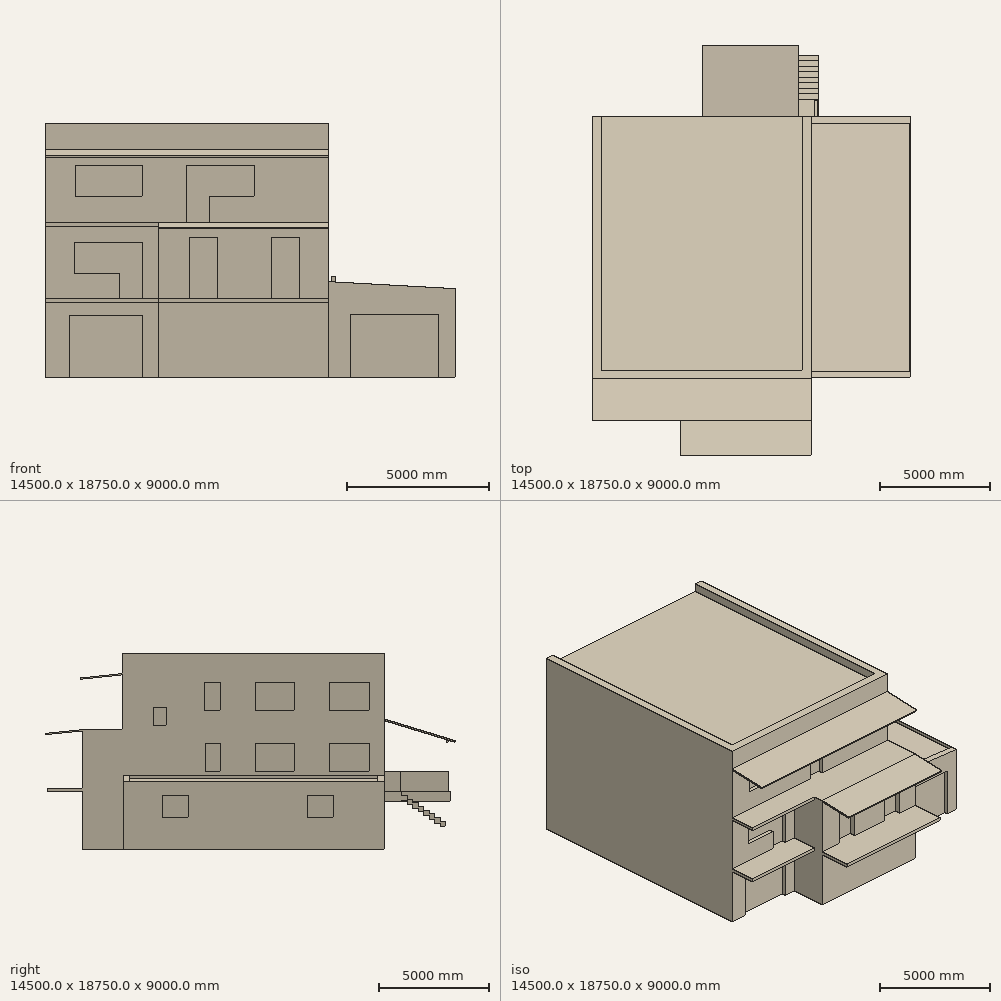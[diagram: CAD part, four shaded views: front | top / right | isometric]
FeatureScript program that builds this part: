
annotation { "Feature Type Name" : "Feature", "Feature Type Description" : "" }
export const myFeature = defineFeature(function(context is Context, id is Id, definition is map)
    precondition{}
    {
        {
            var Q0;
            Q0=qCreatedBy(makeId("Top.planeOp"),FACE);
            var sketch = newSketch(context, id + "F0", { "sketchPlane" : qUnion([Q0])});
            skLineSegment(sketch, "E0.bottom", {"start": v(-4506.26, 6009.06) * mm, "end": v(5493.74, 6009.06) * mm});
            skLineSegment(sketch, "E0.top", {"start": v(-4506.26, -5990.94) * mm, "end": v(5493.74, -5990.94) * mm});
            skLineSegment(sketch, "E0.left", {"start": v(-4506.26, 6009.06) * mm, "end": v(-4506.26, -5990.94) * mm});
            skLineSegment(sketch, "E0.right", {"start": v(5493.74, 6009.06) * mm, "end": v(5493.74, -5990.94) * mm});
            skLineSegment(sketch, "E1.bottom", {"start": v(5493.74, 6009.06) * mm, "end": v(9993.74, 6009.06) * mm});
            skLineSegment(sketch, "E1.top", {"start": v(5493.74, -5940.94) * mm, "end": v(9993.74, -5940.94) * mm});
            skLineSegment(sketch, "E1.left", {"start": v(5493.74, 6009.06) * mm, "end": v(5493.74, -5940.94) * mm});
            skLineSegment(sketch, "E1.right", {"start": v(9993.74, 6009.06) * mm, "end": v(9993.74, -5940.94) * mm});
            skSolve(sketch);
        }
        {
            var Q0;
            Q0=makeQuery(id+"F0.imprint","IMPRINT",FACE,{"disambiguationData":[TD([[makeQuery(id+"F0.imprint","IMPRINT",EDGE,{"derivedFrom":sQuery(id+"F0.wireOp",EDGE,"E0.bottom")}),-1.0]])]});
            extrude(context, id + "F1", {"entities" : qUnion([Q0]), "depth" : 9000 * mm});
        }
        {
            var Q0;
            Q0=makeQuery(id+"F0.imprint","IMPRINT",FACE,{"disambiguationData":[TD([[makeQuery(id+"F0.imprint","IMPRINT",EDGE,{"derivedFrom":sQuery(id+"F0.wireOp",EDGE,"E1.bottom")}),-1.0]])]});
            extrude(context, id + "F2", {"entities" : qUnion([Q0]), "operationType" : NewBodyOperationType.ADD, "depth" : 3400 * mm});
        }
        {
            var Q0;
            Q0=makeQuery(id+"F2.opExtrude","SWEPT_FACE",FACE,{"disambiguationData":[OSD([sQuery(id+"F0.wireOp",EDGE,"E1.top")])]});
            var sketch = newSketch(context, id + "F3", { "sketchPlane" : qUnion([Q0])});
            skLineSegment(sketch, "E2", {"start": v(5493.74, 3400) * mm, "end": v(9993.74, 3400) * mm});
            skLineSegment(sketch, "E3", {"start": v(9993.74, 3400) * mm, "end": v(9993.74, 3150) * mm});
            skLineSegment(sketch, "E4", {"start": v(9993.74, 3150) * mm, "end": v(5493.74, 3400) * mm});
            skSolve(sketch);
        }
        {
            var Q0;
            Q0=makeQuery(id+"F3.imprint","IMPRINT",FACE,{"disambiguationData":[TD([[makeQuery(id+"F3.imprint","IMPRINT",EDGE,{"derivedFrom":sQuery(id+"F3.wireOp",EDGE,"E2")}),-1.0]])]});
            extrude(context, id + "F4", {"entities" : qUnion([Q0]), "operationType" : NewBodyOperationType.REMOVE, "endBound" : BoundingType.THROUGH_ALL, "oppositeDirection" : true, "depth" : 25 * mm});
        }
        {
            var Q0;
            Q0=makeQuery(id+"F4.boolean.opBoolean","COPY",FACE,{"derivedFrom":makeQuery(id+"F4.opExtrude","SWEPT_FACE",FACE,{"disambiguationData":[OSD([sQuery(id+"F3.wireOp",EDGE,"E4")])]})});
            var sketch = newSketch(context, id + "F5", { "sketchPlane" : qUnion([Q0])});
            skLineSegment(sketch, "E5.bottom", {"start": v(9803.62, 5709.06) * mm, "end": v(5296.68, 5709.06) * mm});
            skLineSegment(sketch, "E5.top", {"start": v(9803.62, -5640.94) * mm, "end": v(5296.68, -5640.94) * mm});
            skLineSegment(sketch, "E5.left", {"start": v(9803.62, 5709.06) * mm, "end": v(9803.62, -5640.94) * mm});
            skLineSegment(sketch, "E5.right", {"start": v(5296.68, 5709.06) * mm, "end": v(5296.68, -5640.94) * mm});
            skSolve(sketch);
        }
        {
            var Q0;
            Q0=makeQuery(id+"F5.imprint","IMPRINT",FACE,{"disambiguationData":[TD([[makeQuery(id+"F5.imprint","IMPRINT",EDGE,{"derivedFrom":sQuery(id+"F5.wireOp",EDGE,"E5.bottom")}),1.0]])]});
            extrude(context, id + "F6", {"entities" : qUnion([Q0]), "operationType" : NewBodyOperationType.REMOVE, "oppositeDirection" : true, "depth" : 150 * mm});
        }
        {
            var Q0;
            Q0=makeQuery(id+"F2.opExtrude","SWEPT_FACE",FACE,{"disambiguationData":[OSD([sQuery(id+"F0.wireOp",EDGE,"E1.top")])]});
            var sketch = newSketch(context, id + "F7", { "sketchPlane" : qUnion([Q0])});
            skLineSegment(sketch, "E6.bottom", {"start": v(6293.74, 0) * mm, "end": v(9393.74, 0) * mm});
            skLineSegment(sketch, "E6.top", {"start": v(6293.74, 2250) * mm, "end": v(9393.74, 2250) * mm});
            skLineSegment(sketch, "E6.left", {"start": v(6293.74, 0) * mm, "end": v(6293.74, 2250) * mm});
            skLineSegment(sketch, "E6.right", {"start": v(9393.74, 0) * mm, "end": v(9393.74, 2250) * mm});
            skSolve(sketch);
        }
        {
            var Q0;
            Q0=makeQuery(id+"F7.imprint","IMPRINT",FACE,{"disambiguationData":[TD([[makeQuery(id+"F7.imprint","IMPRINT",EDGE,{"derivedFrom":sQuery(id+"F7.wireOp",EDGE,"E6.bottom")}),1.0]])]});
            extrude(context, id + "F8", {"entities" : qUnion([Q0]), "operationType" : NewBodyOperationType.REMOVE, "oppositeDirection" : true, "depth" : 150 * mm});
        }
        {
            var Q0;
            Q0=makeQuery(id+"F1.opExtrude","SWEPT_FACE",FACE,{"disambiguationData":[OSD([sQuery(id+"F0.wireOp",EDGE,"E0.top")])]});
            var sketch = newSketch(context, id + "F9", { "sketchPlane" : qUnion([Q0])});
            skLineSegment(sketch, "E7.bottom", {"start": v(5493.74, 0) * mm, "end": v(-506.26, 0) * mm});
            skLineSegment(sketch, "E7.top", {"start": v(5493.74, 5500) * mm, "end": v(-506.26, 5500) * mm});
            skLineSegment(sketch, "E7.left", {"start": v(5493.74, 0) * mm, "end": v(5493.74, 5500) * mm});
            skLineSegment(sketch, "E7.right", {"start": v(-506.26, 0) * mm, "end": v(-506.26, 5500) * mm});
            skSolve(sketch);
        }
        {
            var Q0;
            Q0 = qSketchRegion(id + "F9", true);
            extrude(context, id + "F10", {"entities" : qUnion([Q0]), "operationType" : NewBodyOperationType.ADD, "depth" : 1800 * mm});
        }
        {
            var Q0;
            Q0=makeQuery(id+"F10.opExtrude","CAP_FACE",FACE,{"disambiguationData":[OSD([sQuery(id+"F9.wireOp",EDGE,"E7.bottom"),sQuery(id+"F9.wireOp",EDGE,"E7.top"),sQuery(id+"F9.wireOp",EDGE,"E7.left"),sQuery(id+"F9.wireOp",EDGE,"E7.right")])],"isStart":false});
            var sketch = newSketch(context, id + "F11", { "sketchPlane" : qUnion([Q0])});
            skLineSegment(sketch, "E8.bottom", {"start": v(5493.74, 2800) * mm, "end": v(-506.26, 2800) * mm});
            skLineSegment(sketch, "E8.top", {"start": v(5493.74, 2650) * mm, "end": v(-506.26, 2650) * mm});
            skLineSegment(sketch, "E8.left", {"start": v(5493.74, 2800) * mm, "end": v(5493.74, 2650) * mm});
            skLineSegment(sketch, "E8.right", {"start": v(-506.26, 2800) * mm, "end": v(-506.26, 2650) * mm});
            skLineSegment(sketch, "E9.bottom", {"start": v(-506.26, 5500) * mm, "end": v(5493.74, 5500) * mm});
            skLineSegment(sketch, "E9.top", {"start": v(-506.26, 5350) * mm, "end": v(5493.74, 5350) * mm});
            skLineSegment(sketch, "E9.left", {"start": v(-506.26, 5500) * mm, "end": v(-506.26, 5350) * mm});
            skLineSegment(sketch, "E9.right", {"start": v(5493.74, 5500) * mm, "end": v(5493.74, 5350) * mm});
            skSolve(sketch);
        }
        {
            var Q0;
            Q0=makeQuery(id+"F11.imprint","IMPRINT",FACE,{"disambiguationData":[TD([[makeQuery(id+"F11.imprint","IMPRINT",EDGE,{"derivedFrom":sQuery(id+"F11.wireOp",EDGE,"E8.bottom")}),1.0]])]});
            extrude(context, id + "F12", {"entities" : qUnion([Q0]), "operationType" : NewBodyOperationType.ADD, "depth" : 1600 * mm});
        }
        {
            var Q0;
            Q0=makeQuery(id+"F1.opExtrude","SWEPT_FACE",FACE,{"disambiguationData":[OSD([sQuery(id+"F0.wireOp",EDGE,"E0.top")])]});
            var sketch = newSketch(context, id + "F13", { "sketchPlane" : qUnion([Q0])});
            skLineSegment(sketch, "E10.bottom", {"start": v(-506.26, 5500) * mm, "end": v(-4506.26, 5500) * mm});
            skLineSegment(sketch, "E10.top", {"start": v(-506.26, 5350) * mm, "end": v(-4506.26, 5350) * mm});
            skLineSegment(sketch, "E10.left", {"start": v(-506.26, 5500) * mm, "end": v(-506.26, 5350) * mm});
            skLineSegment(sketch, "E10.right", {"start": v(-4506.26, 5500) * mm, "end": v(-4506.26, 5350) * mm});
            skLineSegment(sketch, "E11.bottom", {"start": v(-4506.26, 2800) * mm, "end": v(-506.26, 2800) * mm});
            skLineSegment(sketch, "E11.top", {"start": v(-4506.26, 2650) * mm, "end": v(-506.26, 2650) * mm});
            skLineSegment(sketch, "E11.left", {"start": v(-4506.26, 2800) * mm, "end": v(-4506.26, 2650) * mm});
            skLineSegment(sketch, "E11.right", {"start": v(-506.26, 2800) * mm, "end": v(-506.26, 2650) * mm});
            skSolve(sketch);
        }
        {
            var Q0;
            Q0=makeQuery(id+"F13.imprint","IMPRINT",FACE,{"disambiguationData":[TD([[makeQuery(id+"F13.imprint","IMPRINT",EDGE,{"derivedFrom":sQuery(id+"F13.wireOp",EDGE,"E10.bottom")}),1.0]])]});
            var Q1;
            Q1=makeQuery(id+"F13.imprint","IMPRINT",FACE,{"disambiguationData":[TD([[makeQuery(id+"F13.imprint","IMPRINT",EDGE,{"derivedFrom":sQuery(id+"F13.wireOp",EDGE,"E11.bottom")}),-1.0]])]});
            extrude(context, id + "F14", {"entities" : qUnion([Q0, Q1]), "operationType" : NewBodyOperationType.ADD, "depth" : 1300 * mm});
        }
        {
            var Q0;
            Q0=makeQuery(id+"F12.boolean.opBoolean","MERGE",FACE,{"derivedFrom":[makeQuery(id+"F10.boolean.opBoolean","MERGE",FACE,{"derivedFrom":[makeQuery(id+"F1.opExtrude","SWEPT_FACE",FACE,{"disambiguationData":[OSD([sQuery(id+"F0.wireOp",EDGE,"E0.right"),sQuery(id+"F0.wireOp",EDGE,"E1.left")])]}),makeQuery(id+"F10.opExtrude","SWEPT_FACE",FACE,{"disambiguationData":[OSD([sQuery(id+"F9.wireOp",EDGE,"E7.left")])]})]}),makeQuery(id+"F12.opExtrude","SWEPT_FACE",FACE,{"disambiguationData":[OSD([sQuery(id+"F11.wireOp",EDGE,"E8.left")])]}),makeQuery(id+"F12.opExtrude","SWEPT_FACE",FACE,{"disambiguationData":[OSD([sQuery(id+"F11.wireOp",EDGE,"E9.right")])]})]});
            var sketch = newSketch(context, id + "F15", { "sketchPlane" : qUnion([Q0])});
            skLineSegment(sketch, "E12.bottom", {"start": v(-2190.94, 4867.43) * mm, "end": v(-1490.94, 4867.43) * mm});
            skLineSegment(sketch, "E12.top", {"start": v(-2190.94, 3567.43) * mm, "end": v(-1490.94, 3567.43) * mm});
            skLineSegment(sketch, "E12.left", {"start": v(-2190.94, 4867.43) * mm, "end": v(-2190.94, 3567.43) * mm});
            skLineSegment(sketch, "E12.right", {"start": v(-1490.94, 4867.43) * mm, "end": v(-1490.94, 3567.43) * mm});
            skLineSegment(sketch, "E13.bottom", {"start": v(109.06, 4867.43) * mm, "end": v(1909.06, 4867.43) * mm});
            skLineSegment(sketch, "E13.top", {"start": v(109.06, 3567.43) * mm, "end": v(1909.06, 3567.43) * mm});
            skLineSegment(sketch, "E13.left", {"start": v(109.06, 4867.43) * mm, "end": v(109.06, 3567.43) * mm});
            skLineSegment(sketch, "E13.right", {"start": v(1909.06, 4867.43) * mm, "end": v(1909.06, 3567.43) * mm});
            skLineSegment(sketch, "E14.bottom", {"start": v(3509.06, 4867.43) * mm, "end": v(5309.06, 4867.43) * mm});
            skLineSegment(sketch, "E14.top", {"start": v(3509.06, 3567.43) * mm, "end": v(5309.06, 3567.43) * mm});
            skLineSegment(sketch, "E14.left", {"start": v(3509.06, 4867.43) * mm, "end": v(3509.06, 3567.43) * mm});
            skLineSegment(sketch, "E14.right", {"start": v(5309.06, 4867.43) * mm, "end": v(5309.06, 3567.43) * mm});
            skLineSegment(sketch, "E15.bottom", {"start": v(109.06, 6367.43) * mm, "end": v(1909.06, 6367.43) * mm});
            skLineSegment(sketch, "E15.top", {"start": v(109.06, 7667.43) * mm, "end": v(1909.06, 7667.43) * mm});
            skLineSegment(sketch, "E15.left", {"start": v(109.06, 6367.43) * mm, "end": v(109.06, 7667.43) * mm});
            skLineSegment(sketch, "E15.right", {"start": v(1909.06, 6367.43) * mm, "end": v(1909.06, 7667.43) * mm});
            skLineSegment(sketch, "E16.bottom", {"start": v(3509.06, 6367.43) * mm, "end": v(5309.06, 6367.43) * mm});
            skLineSegment(sketch, "E16.top", {"start": v(3509.06, 7667.43) * mm, "end": v(5309.06, 7667.43) * mm});
            skLineSegment(sketch, "E16.left", {"start": v(3509.06, 6367.43) * mm, "end": v(3509.06, 7667.43) * mm});
            skLineSegment(sketch, "E16.right", {"start": v(5309.06, 6367.43) * mm, "end": v(5309.06, 7667.43) * mm});
            skLineSegment(sketch, "E17.bottom", {"start": v(-1490.94, 6367.43) * mm, "end": v(-2240.55, 6367.43) * mm});
            skLineSegment(sketch, "E17.top", {"start": v(-1490.94, 7667.43) * mm, "end": v(-2240.55, 7667.43) * mm});
            skLineSegment(sketch, "E17.left", {"start": v(-1490.94, 6367.43) * mm, "end": v(-1490.94, 7667.43) * mm});
            skLineSegment(sketch, "E17.right", {"start": v(-2240.55, 6367.43) * mm, "end": v(-2240.55, 7667.43) * mm});
            skLineSegment(sketch, "E18.bottom", {"start": v(-4545.24, 6502.32) * mm, "end": v(-3968.61, 6502.32) * mm});
            skLineSegment(sketch, "E18.top", {"start": v(-4545.24, 5695.04) * mm, "end": v(-3968.61, 5695.04) * mm});
            skLineSegment(sketch, "E18.left", {"start": v(-4545.24, 6502.32) * mm, "end": v(-4545.24, 5695.04) * mm});
            skLineSegment(sketch, "E18.right", {"start": v(-3968.61, 6502.32) * mm, "end": v(-3968.61, 5695.04) * mm});
            skSolve(sketch);
        }
        {
            var Q0;
            Q0=makeQuery(id+"F15.imprint","IMPRINT",FACE,{"disambiguationData":[TD([[makeQuery(id+"F15.imprint","IMPRINT",EDGE,{"derivedFrom":sQuery(id+"F15.wireOp",EDGE,"E18.bottom")}),-1.0]])]});
            var Q1;
            Q1=makeQuery(id+"F15.imprint","IMPRINT",FACE,{"disambiguationData":[TD([[makeQuery(id+"F15.imprint","IMPRINT",EDGE,{"derivedFrom":sQuery(id+"F15.wireOp",EDGE,"E17.bottom")}),-1.0]])]});
            var Q2;
            Q2=makeQuery(id+"F15.imprint","IMPRINT",FACE,{"disambiguationData":[TD([[makeQuery(id+"F15.imprint","IMPRINT",EDGE,{"derivedFrom":sQuery(id+"F15.wireOp",EDGE,"E15.bottom")}),1.0]])]});
            var Q3;
            Q3=makeQuery(id+"F15.imprint","IMPRINT",FACE,{"disambiguationData":[TD([[makeQuery(id+"F15.imprint","IMPRINT",EDGE,{"derivedFrom":sQuery(id+"F15.wireOp",EDGE,"E16.bottom")}),1.0]])]});
            var Q4;
            Q4=makeQuery(id+"F15.imprint","IMPRINT",FACE,{"disambiguationData":[TD([[makeQuery(id+"F15.imprint","IMPRINT",EDGE,{"derivedFrom":sQuery(id+"F15.wireOp",EDGE,"E14.bottom")}),-1.0]])]});
            var Q5;
            Q5=makeQuery(id+"F15.imprint","IMPRINT",FACE,{"disambiguationData":[TD([[makeQuery(id+"F15.imprint","IMPRINT",EDGE,{"derivedFrom":sQuery(id+"F15.wireOp",EDGE,"E13.bottom")}),-1.0]])]});
            var Q6;
            Q6=makeQuery(id+"F15.imprint","IMPRINT",FACE,{"disambiguationData":[TD([[makeQuery(id+"F15.imprint","IMPRINT",EDGE,{"derivedFrom":sQuery(id+"F15.wireOp",EDGE,"E12.bottom")}),-1.0]])]});
            extrude(context, id + "F16", {"entities" : qUnion([Q0, Q1, Q2, Q3, Q4, Q5, Q6]), "operationType" : NewBodyOperationType.REMOVE, "oppositeDirection" : true, "depth" : 200 * mm});
        }
        {
            var Q0;
            Q0=makeQuery(id+"F2.opExtrude","SWEPT_FACE",FACE,{"disambiguationData":[OSD([sQuery(id+"F0.wireOp",EDGE,"E1.right")])]});
            var sketch = newSketch(context, id + "F17", { "sketchPlane" : qUnion([Q0])});
            skLineSegment(sketch, "E19.bottom", {"start": v(-4154.46, 2500) * mm, "end": v(-2954.46, 2500) * mm});
            skLineSegment(sketch, "E19.top", {"start": v(-4154.46, 1500) * mm, "end": v(-2954.46, 1500) * mm});
            skLineSegment(sketch, "E19.left", {"start": v(-4154.46, 2500) * mm, "end": v(-4154.46, 1500) * mm});
            skLineSegment(sketch, "E19.right", {"start": v(-2954.46, 2500) * mm, "end": v(-2954.46, 1500) * mm});
            skLineSegment(sketch, "E20.bottom", {"start": v(2485.6, 2500) * mm, "end": v(3685.6, 2500) * mm});
            skLineSegment(sketch, "E20.top", {"start": v(2485.6, 1500) * mm, "end": v(3685.6, 1500) * mm});
            skLineSegment(sketch, "E20.left", {"start": v(2485.6, 2500) * mm, "end": v(2485.6, 1500) * mm});
            skLineSegment(sketch, "E20.right", {"start": v(3685.6, 2500) * mm, "end": v(3685.6, 1500) * mm});
            skSolve(sketch);
        }
        {
            var Q0;
            Q0=makeQuery(id+"F17.imprint","IMPRINT",FACE,{"disambiguationData":[TD([[makeQuery(id+"F17.imprint","IMPRINT",EDGE,{"derivedFrom":sQuery(id+"F17.wireOp",EDGE,"E19.bottom")}),-1.0]])]});
            var Q1;
            Q1=makeQuery(id+"F17.imprint","IMPRINT",FACE,{"disambiguationData":[TD([[makeQuery(id+"F17.imprint","IMPRINT",EDGE,{"derivedFrom":sQuery(id+"F17.wireOp",EDGE,"E20.bottom")}),-1.0]])]});
            extrude(context, id + "F18", {"entities" : qUnion([Q0, Q1]), "operationType" : NewBodyOperationType.REMOVE, "oppositeDirection" : true, "depth" : 200 * mm});
        }
        {
            var Q0;
            {var subQ2=sQuery(id+"F0.wireOp",EDGE,"E0.top");Q0=makeQuery(id+"F14.boolean.opBoolean","SPLIT",FACE,{"disambiguationData":[TD([makeQuery(id+"F10.opExtrude","SWEPT_FACE",FACE,{"disambiguationData":[OSD([sQuery(id+"F9.wireOp",EDGE,"E7.bottom")])]})])],"derivedFrom":makeQuery(id+"F1.opExtrude","SWEPT_FACE",FACE,{"disambiguationData":[OSD([subQ2])]})});}
            var sketch = newSketch(context, id + "F19", { "sketchPlane" : qUnion([Q0])});
            skLineSegment(sketch, "E21.bottom", {"start": v(-3641.41, 2200) * mm, "end": v(-1090.82, 2200) * mm});
            skLineSegment(sketch, "E21.top", {"start": v(-3641.41, 0) * mm, "end": v(-1090.82, 0) * mm});
            skLineSegment(sketch, "E21.left", {"start": v(-3641.41, 2200) * mm, "end": v(-3641.41, 0) * mm});
            skLineSegment(sketch, "E21.right", {"start": v(-1090.82, 2200) * mm, "end": v(-1090.82, 0) * mm});
            skSolve(sketch);
        }
        {
            var Q0;
            Q0=makeQuery(id+"F19.imprint","IMPRINT",FACE,{"disambiguationData":[TD([[makeQuery(id+"F19.imprint","IMPRINT",EDGE,{"derivedFrom":sQuery(id+"F19.wireOp",EDGE,"E21.bottom")}),-1.0]])]});
            extrude(context, id + "F20", {"entities" : qUnion([Q0]), "operationType" : NewBodyOperationType.REMOVE, "oppositeDirection" : true, "depth" : 200 * mm});
        }
        {
            var Q0;
            Q0=makeQuery(id+"F1.opExtrude","CAP_FACE",FACE,{"disambiguationData":[OSD([sQuery(id+"F0.wireOp",EDGE,"E0.bottom"),sQuery(id+"F0.wireOp",EDGE,"E0.top"),sQuery(id+"F0.wireOp",EDGE,"E0.left"),sQuery(id+"F0.wireOp",EDGE,"E0.right"),sQuery(id+"F0.wireOp",EDGE,"E1.left")])],"isStart":false});
            var sketch = newSketch(context, id + "F21", { "sketchPlane" : qUnion([Q0])});
            skLineSegment(sketch, "E22.bottom", {"start": v(-4106.26, 6009.06) * mm, "end": v(5093.74, 6009.06) * mm});
            skLineSegment(sketch, "E22.top", {"start": v(-4106.26, -5590.94) * mm, "end": v(5093.74, -5590.94) * mm});
            skLineSegment(sketch, "E22.left", {"start": v(-4106.26, 6009.06) * mm, "end": v(-4106.26, -5590.94) * mm});
            skLineSegment(sketch, "E22.right", {"start": v(5093.74, 6009.06) * mm, "end": v(5093.74, -5590.94) * mm});
            skSolve(sketch);
        }
        {
            var Q0;
            Q0 = qSketchRegion(id + "F21", true);
            extrude(context, id + "F22", {"entities" : qUnion([Q0]), "operationType" : NewBodyOperationType.REMOVE, "oppositeDirection" : true, "depth" : 400 * mm});
        }
        {
            var Q0;
            {var subQ0=sQuery(id+"F9.wireOp",EDGE,"E7.left");var subQ1=sQuery(id+"F9.wireOp",EDGE,"E7.right");Q0=makeQuery(id+"F12.boolean.opBoolean","SPLIT",FACE,{"disambiguationData":[TD([makeQuery(id+"F12.opExtrude","SWEPT_FACE",FACE,{"disambiguationData":[OSD([sQuery(id+"F11.wireOp",EDGE,"E8.bottom")])]})])],"derivedFrom":makeQuery(id+"F10.opExtrude","CAP_FACE",FACE,{"disambiguationData":[OSD([sQuery(id+"F9.wireOp",EDGE,"E7.bottom"),sQuery(id+"F9.wireOp",EDGE,"E7.top"),subQ0,subQ1])],"isStart":false})});}
            var sketch = newSketch(context, id + "F23", { "sketchPlane" : qUnion([Q0])});
            skLineSegment(sketch, "E23.bottom", {"start": v(581.4, 4950) * mm, "end": v(1581.4, 4950) * mm});
            skLineSegment(sketch, "E23.top", {"start": v(581.4, 2800) * mm, "end": v(1581.4, 2800) * mm});
            skLineSegment(sketch, "E23.left", {"start": v(581.4, 4950) * mm, "end": v(581.4, 2800) * mm});
            skLineSegment(sketch, "E23.right", {"start": v(1581.4, 4950) * mm, "end": v(1581.4, 2800) * mm});
            skLineSegment(sketch, "E24.bottom", {"start": v(3481.4, 2800) * mm, "end": v(4481.4, 2800) * mm});
            skLineSegment(sketch, "E24.top", {"start": v(3481.4, 4950) * mm, "end": v(4481.4, 4950) * mm});
            skLineSegment(sketch, "E24.left", {"start": v(3481.4, 2800) * mm, "end": v(3481.4, 4950) * mm});
            skLineSegment(sketch, "E24.right", {"start": v(4481.4, 2800) * mm, "end": v(4481.4, 4950) * mm});
            skSolve(sketch);
        }
        {
            var Q0;
            Q0=makeQuery(id+"F23.imprint","IMPRINT",FACE,{"disambiguationData":[TD([[makeQuery(id+"F23.imprint","IMPRINT",EDGE,{"derivedFrom":sQuery(id+"F23.wireOp",EDGE,"E24.bottom")}),-1.0]])]});
            var Q1;
            Q1=makeQuery(id+"F23.imprint","IMPRINT",FACE,{"disambiguationData":[TD([[makeQuery(id+"F23.imprint","IMPRINT",EDGE,{"derivedFrom":sQuery(id+"F23.wireOp",EDGE,"E23.bottom")}),-1.0]])]});
            extrude(context, id + "F24", {"entities" : qUnion([Q0, Q1]), "operationType" : NewBodyOperationType.REMOVE, "oppositeDirection" : true, "depth" : 300 * mm});
        }
        {
            var Q0;
            {var subQ3=sQuery(id+"F0.wireOp",EDGE,"E0.top");Q0=makeQuery(id+"F14.boolean.opBoolean","SPLIT",FACE,{"disambiguationData":[TD([makeQuery(id+"F10.opExtrude","SWEPT_FACE",FACE,{"disambiguationData":[OSD([sQuery(id+"F9.wireOp",EDGE,"E7.top")])]})])],"derivedFrom":makeQuery(id+"F1.opExtrude","SWEPT_FACE",FACE,{"disambiguationData":[OSD([subQ3])]})});}
            var sketch = newSketch(context, id + "F25", { "sketchPlane" : qUnion([Q0])});
            skLineSegment(sketch, "E25.bottom", {"start": v(2893.74, 7500) * mm, "end": v(1293.74, 7500) * mm});
            skLineSegment(sketch, "E25.top", {"start": v(2893.74, 6400) * mm, "end": v(1293.74, 6400) * mm});
            skLineSegment(sketch, "E25.left", {"start": v(2893.74, 7500) * mm, "end": v(2893.74, 6400) * mm});
            skLineSegment(sketch, "E25.right", {"start": v(1293.74, 7500) * mm, "end": v(1293.74, 6400) * mm});
            skLineSegment(sketch, "E26.bottom", {"start": v(1293.74, 7500) * mm, "end": v(493.74, 7500) * mm});
            skLineSegment(sketch, "E26.top", {"start": v(1293.74, 5500) * mm, "end": v(493.74, 5500) * mm});
            skLineSegment(sketch, "E26.left", {"start": v(1293.74, 7500) * mm, "end": v(1293.74, 5500) * mm});
            skLineSegment(sketch, "E26.right", {"start": v(493.74, 7500) * mm, "end": v(493.74, 5500) * mm});
            skLineSegment(sketch, "E27.bottom", {"start": v(-1088.33, 6400) * mm, "end": v(-3428.85, 6400) * mm});
            skLineSegment(sketch, "E27.top", {"start": v(-1088.33, 7500) * mm, "end": v(-3428.85, 7500) * mm});
            skLineSegment(sketch, "E27.left", {"start": v(-1088.33, 6400) * mm, "end": v(-1088.33, 7500) * mm});
            skLineSegment(sketch, "E27.right", {"start": v(-3428.85, 6400) * mm, "end": v(-3428.85, 7500) * mm});
            skLineSegment(sketch, "E28.bottom", {"start": v(-1088.33, 4800) * mm, "end": v(-1888.33, 4800) * mm});
            skLineSegment(sketch, "E28.top", {"start": v(-1088.33, 2800) * mm, "end": v(-1888.33, 2800) * mm});
            skLineSegment(sketch, "E28.left", {"start": v(-1088.33, 4800) * mm, "end": v(-1088.33, 2800) * mm});
            skLineSegment(sketch, "E28.right", {"start": v(-1888.33, 4800) * mm, "end": v(-1888.33, 2800) * mm});
            skLineSegment(sketch, "E29.bottom", {"start": v(-3488.33, 4800) * mm, "end": v(-1888.33, 4800) * mm});
            skLineSegment(sketch, "E29.top", {"start": v(-3488.33, 3700) * mm, "end": v(-1888.33, 3700) * mm});
            skLineSegment(sketch, "E29.left", {"start": v(-3488.33, 4800) * mm, "end": v(-3488.33, 3700) * mm});
            skLineSegment(sketch, "E29.right", {"start": v(-1888.33, 4800) * mm, "end": v(-1888.33, 3700) * mm});
            skSolve(sketch);
        }
        {
            var Q0;
            Q0=makeQuery(id+"F25.imprint","IMPRINT",FACE,{"disambiguationData":[TD([[makeQuery(id+"F25.imprint","IMPRINT",EDGE,{"derivedFrom":sQuery(id+"F25.wireOp",EDGE,"E27.bottom")}),-1.0]])]});
            var Q1;
            {var subQ1=sQuery(id+"F25.wireOp",EDGE,"E26.bottom");Q1=makeQuery(id+"F25.imprint","IMPRINT",FACE,{"disambiguationData":[TD([[makeQuery(id+"F25.imprint","IMPRINT",EDGE,{"derivedFrom":subQ1}),1.0]])]});}
            var Q2;
            {var subQ0=sQuery(id+"F25.wireOp",EDGE,"E25.bottom");Q2=makeQuery(id+"F25.imprint","IMPRINT",FACE,{"disambiguationData":[TD([[makeQuery(id+"F25.imprint","IMPRINT",EDGE,{"derivedFrom":subQ0}),1.0]])]});}
            var Q3;
            Q3=makeQuery(id+"F25.imprint","IMPRINT",FACE,{"disambiguationData":[TD([[makeQuery(id+"F25.imprint","IMPRINT",EDGE,{"derivedFrom":sQuery(id+"F25.wireOp",EDGE,"E28.bottom")}),1.0]])]});
            var Q4;
            Q4=makeQuery(id+"F25.imprint","IMPRINT",FACE,{"disambiguationData":[TD([[makeQuery(id+"F25.imprint","IMPRINT",EDGE,{"derivedFrom":sQuery(id+"F25.wireOp",EDGE,"E29.bottom")}),-1.0]])]});
            extrude(context, id + "F26", {"entities" : qUnion([Q0, Q1, Q2, Q3, Q4]), "operationType" : NewBodyOperationType.REMOVE, "oppositeDirection" : true, "depth" : 200 * mm});
        }
        {
            var Q0;
            Q0=makeQuery(id+"F12.boolean.opBoolean","MERGE",FACE,{"derivedFrom":[makeQuery(id+"F10.boolean.opBoolean","MERGE",FACE,{"derivedFrom":[makeQuery(id+"F1.opExtrude","SWEPT_FACE",FACE,{"disambiguationData":[OSD([sQuery(id+"F0.wireOp",EDGE,"E0.right"),sQuery(id+"F0.wireOp",EDGE,"E1.left")])]}),makeQuery(id+"F10.opExtrude","SWEPT_FACE",FACE,{"disambiguationData":[OSD([sQuery(id+"F9.wireOp",EDGE,"E7.left")])]})]}),makeQuery(id+"F12.opExtrude","SWEPT_FACE",FACE,{"disambiguationData":[OSD([sQuery(id+"F11.wireOp",EDGE,"E8.left")])]}),makeQuery(id+"F12.opExtrude","SWEPT_FACE",FACE,{"disambiguationData":[OSD([sQuery(id+"F11.wireOp",EDGE,"E9.right")])]})]});
            var sketch = newSketch(context, id + "F27", { "sketchPlane" : qUnion([Q0])});
            skLineSegment(sketch, "E30", {"start": v(-5990.94, 8059.67) * mm, "end": v(-7890.94, 7859.67) * mm});
            skLineSegment(sketch, "E31", {"start": v(-7890.94, 7859.67) * mm, "end": v(-7884.66, 7800) * mm});
            skLineSegment(sketch, "E32", {"start": v(-7884.66, 7800) * mm, "end": v(-5990.94, 7999.34) * mm});
            skSolve(sketch);
        }
        {
            var Q0;
            {var subQ0=sQuery(id+"F27.wireOp",EDGE,"E30");Q0=makeQuery(id+"F27.imprint","IMPRINT",FACE,{"disambiguationData":[TD([[makeQuery(id+"F27.imprint","IMPRINT",EDGE,{"derivedFrom":subQ0}),1.0]])]});}
            var Q1;
            Q1=makeQuery(id+"F14.boolean.opBoolean","MERGE",FACE,{"derivedFrom":[makeQuery(id+"F1.opExtrude","SWEPT_FACE",FACE,{"disambiguationData":[OSD([sQuery(id+"F0.wireOp",EDGE,"E0.left")])]}),makeQuery(id+"F14.opExtrude","SWEPT_FACE",FACE,{"disambiguationData":[OSD([sQuery(id+"F13.wireOp",EDGE,"E10.right")])]}),makeQuery(id+"F14.opExtrude","SWEPT_FACE",FACE,{"disambiguationData":[OSD([sQuery(id+"F13.wireOp",EDGE,"E11.left")])]})]});
            extrude(context, id + "F28", {"entities" : qUnion([Q0]), "operationType" : NewBodyOperationType.ADD, "endBound" : BoundingType.UP_TO_SURFACE, "oppositeDirection" : true, "endBoundEntityFace" : qUnion([Q1]), "depth" : 25 * mm});
        }
        {
            var Q0;
            {var subQ0=sQuery(id+"F0.wireOp",EDGE,"E0.right");Q0=makeQuery(id+"F28.boolean.opBoolean","MERGE",FACE,{"derivedFrom":[makeQuery(id+"F12.boolean.opBoolean","MERGE",FACE,{"derivedFrom":[makeQuery(id+"F10.boolean.opBoolean","MERGE",FACE,{"derivedFrom":[makeQuery(id+"F1.opExtrude","SWEPT_FACE",FACE,{"disambiguationData":[OSD([subQ0,sQuery(id+"F0.wireOp",EDGE,"E1.left")])]}),makeQuery(id+"F10.opExtrude","SWEPT_FACE",FACE,{"disambiguationData":[OSD([sQuery(id+"F9.wireOp",EDGE,"E7.left")])]})]}),makeQuery(id+"F12.opExtrude","SWEPT_FACE",FACE,{"disambiguationData":[OSD([sQuery(id+"F11.wireOp",EDGE,"E8.left")])]})]}),makeQuery(id+"F28.opExtrude","CAP_FACE",FACE,{"disambiguationData":[OSD([sQuery(id+"F0.wireOp",EDGE,"E0.top"),subQ0,sQuery(id+"F27.wireOp",EDGE,"E30"),sQuery(id+"F27.wireOp",EDGE,"E31"),sQuery(id+"F27.wireOp",EDGE,"E32")])],"isStart":true})]});}
            var sketch = newSketch(context, id + "F29", { "sketchPlane" : qUnion([Q0])});
            skLineSegment(sketch, "E33", {"start": v(-7790.94, 5500) * mm, "end": v(-9490.94, 5330) * mm});
            skLineSegment(sketch, "E34", {"start": v(-9490.94, 5330) * mm, "end": v(-9484.97, 5270.3) * mm});
            skLineSegment(sketch, "E35", {"start": v(-9484.97, 5270.3) * mm, "end": v(-7790.94, 5439.7) * mm});
            skSolve(sketch);
        }
        {
            var Q0;
            {var subQ0=sQuery(id+"F29.wireOp",EDGE,"E33");Q0=makeQuery(id+"F29.imprint","IMPRINT",FACE,{"disambiguationData":[TD([[makeQuery(id+"F29.imprint","IMPRINT",EDGE,{"derivedFrom":subQ0}),1.0]])]});}
            var Q1;
            Q1=makeQuery(id+"F12.boolean.opBoolean","MERGE",FACE,{"derivedFrom":[makeQuery(id+"F10.opExtrude","SWEPT_FACE",FACE,{"disambiguationData":[OSD([sQuery(id+"F9.wireOp",EDGE,"E7.right")])]}),makeQuery(id+"F12.opExtrude","SWEPT_FACE",FACE,{"disambiguationData":[OSD([sQuery(id+"F11.wireOp",EDGE,"E8.right")])]})]});
            extrude(context, id + "F30", {"entities" : qUnion([Q0]), "operationType" : NewBodyOperationType.ADD, "endBound" : BoundingType.UP_TO_SURFACE, "oppositeDirection" : true, "endBoundEntityFace" : qUnion([Q1]), "depth" : 25 * mm});
        }
        {
            var Q0;
            Q0=makeQuery(id+"F2.boolean.opBoolean","MERGE",FACE,{"derivedFrom":[makeQuery(id+"F1.opExtrude","SWEPT_FACE",FACE,{"disambiguationData":[OSD([sQuery(id+"F0.wireOp",EDGE,"E0.bottom")])]}),makeQuery(id+"F2.opExtrude","SWEPT_FACE",FACE,{"disambiguationData":[OSD([sQuery(id+"F0.wireOp",EDGE,"E1.bottom")])]})]});
            var sketch = newSketch(context, id + "F31", { "sketchPlane" : qUnion([Q0])});
            skLineSegment(sketch, "E36.bottom", {"start": v(-8108.12, 2400) * mm, "end": v(-6908.12, 2400) * mm});
            skLineSegment(sketch, "E36.top", {"start": v(-8108.12, 1400) * mm, "end": v(-6908.12, 1400) * mm});
            skLineSegment(sketch, "E36.left", {"start": v(-8108.12, 2400) * mm, "end": v(-8108.12, 1400) * mm});
            skLineSegment(sketch, "E36.right", {"start": v(-6908.12, 2400) * mm, "end": v(-6908.12, 1400) * mm});
            skSolve(sketch);
        }
        {
            var Q0;
            Q0=makeQuery(id+"F31.imprint","IMPRINT",FACE,{"disambiguationData":[TD([[makeQuery(id+"F31.imprint","IMPRINT",EDGE,{"derivedFrom":sQuery(id+"F31.wireOp",EDGE,"E36.bottom")}),-1.0]])]});
            extrude(context, id + "F32", {"entities" : qUnion([Q0]), "operationType" : NewBodyOperationType.REMOVE, "oppositeDirection" : true, "depth" : 200 * mm});
        }
        {
            var Q0;
            Q0=makeQuery(id+"F2.boolean.opBoolean","MERGE",FACE,{"derivedFrom":[makeQuery(id+"F1.opExtrude","SWEPT_FACE",FACE,{"disambiguationData":[OSD([sQuery(id+"F0.wireOp",EDGE,"E0.bottom")])]}),makeQuery(id+"F2.opExtrude","SWEPT_FACE",FACE,{"disambiguationData":[OSD([sQuery(id+"F0.wireOp",EDGE,"E1.bottom")])]})]});
            var sketch = newSketch(context, id + "F33", { "sketchPlane" : qUnion([Q0])});
            skPoint(sketch, "E37", {"position": v(-4893.74, 2667.43) * mm});
            skLineSegment(sketch, "E38.bottom", {"start": v(-4893.74, 2667.43) * mm, "end": v(-493.74, 2667.43) * mm});
            skLineSegment(sketch, "E38.top", {"start": v(-4893.74, 2217.43) * mm, "end": v(-493.74, 2217.43) * mm});
            skLineSegment(sketch, "E38.left", {"start": v(-4893.74, 2667.43) * mm, "end": v(-4893.74, 2217.43) * mm});
            skLineSegment(sketch, "E38.right", {"start": v(-493.74, 2667.43) * mm, "end": v(-493.74, 2217.43) * mm});
            skSolve(sketch);
        }
        {
            var Q0;
            Q0 = qSketchRegion(id + "F33", true);
            extrude(context, id + "F34", {"entities" : qUnion([Q0]), "operationType" : NewBodyOperationType.ADD, "depth" : 3000 * mm, "offsetDistance" : 25 * mm});
        }
        {
            var Q0;
            Q0=makeQuery(id+"F2.boolean.opBoolean","MERGE",FACE,{"derivedFrom":[makeQuery(id+"F1.opExtrude","SWEPT_FACE",FACE,{"disambiguationData":[OSD([sQuery(id+"F0.wireOp",EDGE,"E0.bottom")])]}),makeQuery(id+"F2.opExtrude","SWEPT_FACE",FACE,{"disambiguationData":[OSD([sQuery(id+"F0.wireOp",EDGE,"E1.bottom")])]})]});
            var sketch = newSketch(context, id + "F35", { "sketchPlane" : qUnion([Q0])});
            skLineSegment(sketch, "E39.bottom", {"start": v(-3993.74, 2717.43) * mm, "end": v(-2593.74, 2717.43) * mm});
            skLineSegment(sketch, "E39.top", {"start": v(-3993.74, 4817.43) * mm, "end": v(-2593.74, 4817.43) * mm});
            skLineSegment(sketch, "E39.left", {"start": v(-3993.74, 2717.43) * mm, "end": v(-3993.74, 4817.43) * mm});
            skLineSegment(sketch, "E39.right", {"start": v(-2593.74, 2717.43) * mm, "end": v(-2593.74, 4817.43) * mm});
            skSolve(sketch);
        }
        {
            var Q0;
            Q0 = qSketchRegion(id + "F35", true);
            var Q1;
            Q1=makeQuery(id+"F35.imprint","IMPRINT",FACE,{"disambiguationData":[TD([[makeQuery(id+"F35.imprint","IMPRINT",EDGE,{"derivedFrom":sQuery(id+"F35.wireOp",EDGE,"E39.bottom")}),1.0]])]});
            extrude(context, id + "F36", {"entities" : qUnion([Q0, Q1]), "operationType" : NewBodyOperationType.REMOVE, "depth" : -150 * mm, "offsetDistance" : 25 * mm});
        }
        {
            var Q0;
            Q0=makeQuery(id+"F34.opExtrude","SWEPT_FACE",FACE,{"disambiguationData":[OSD([sQuery(id+"F33.wireOp",EDGE,"E38.left")])]});
            var sketch = newSketch(context, id + "F37", { "sketchPlane" : qUnion([Q0])});
            skPoint(sketch, "E40.oppositeSnap0", {"position": v(6009.06, 2217.43) * mm});
            skLineSegment(sketch, "E40.bottom", {"start": v(6009.06, 2667.43) * mm, "end": v(6809.06, 2667.43) * mm});
            skLineSegment(sketch, "E40.top", {"start": v(6009.06, 2217.43) * mm, "end": v(6809.06, 2217.43) * mm});
            skLineSegment(sketch, "E40.left", {"start": v(6009.06, 2667.43) * mm, "end": v(6009.06, 2217.43) * mm});
            skLineSegment(sketch, "E40.right", {"start": v(6809.06, 2667.43) * mm, "end": v(6809.06, 2217.43) * mm});
            skLineSegment(sketch, "E41.bottom", {"start": v(6809.06, 2497.43) * mm, "end": v(7059.06, 2497.43) * mm});
            skLineSegment(sketch, "E41.top", {"start": v(6809.06, 2247.43) * mm, "end": v(7059.06, 2247.43) * mm});
            skLineSegment(sketch, "E41.left", {"start": v(6809.06, 2497.43) * mm, "end": v(6809.06, 2247.43) * mm});
            skLineSegment(sketch, "E41.right", {"start": v(7059.06, 2497.43) * mm, "end": v(7059.06, 2247.43) * mm});
            skLineSegment(sketch, "E42.1.0.0", {"start": v(7309.06, 2327.43) * mm, "end": v(7309.06, 2077.43) * mm});
            skLineSegment(sketch, "E42.1.0.1", {"start": v(7059.06, 2327.43) * mm, "end": v(7309.06, 2327.43) * mm});
            skLineSegment(sketch, "E42.1.0.2", {"start": v(7059.06, 2077.43) * mm, "end": v(7309.06, 2077.43) * mm});
            skLineSegment(sketch, "E42.1.0.3", {"start": v(7059.06, 2327.43) * mm, "end": v(7059.06, 2077.43) * mm});
            skLineSegment(sketch, "E42.2.0.0", {"start": v(7559.06, 2157.43) * mm, "end": v(7559.06, 1907.43) * mm});
            skLineSegment(sketch, "E42.2.0.1", {"start": v(7309.06, 2157.43) * mm, "end": v(7559.06, 2157.43) * mm});
            skLineSegment(sketch, "E42.2.0.2", {"start": v(7309.06, 1907.43) * mm, "end": v(7559.06, 1907.43) * mm});
            skLineSegment(sketch, "E42.2.0.3", {"start": v(7309.06, 2157.43) * mm, "end": v(7309.06, 1907.43) * mm});
            skLineSegment(sketch, "E42.3.0.0", {"start": v(7809.06, 1987.43) * mm, "end": v(7809.06, 1737.43) * mm});
            skLineSegment(sketch, "E42.3.0.1", {"start": v(7559.06, 1987.43) * mm, "end": v(7809.06, 1987.43) * mm});
            skLineSegment(sketch, "E42.3.0.2", {"start": v(7559.06, 1737.43) * mm, "end": v(7809.06, 1737.43) * mm});
            skLineSegment(sketch, "E42.3.0.3", {"start": v(7559.06, 1987.43) * mm, "end": v(7559.06, 1737.43) * mm});
            skLineSegment(sketch, "E42.4.0.0", {"start": v(8059.06, 1817.43) * mm, "end": v(8059.06, 1567.43) * mm});
            skLineSegment(sketch, "E42.4.0.1", {"start": v(7809.06, 1817.43) * mm, "end": v(8059.06, 1817.43) * mm});
            skLineSegment(sketch, "E42.4.0.2", {"start": v(7809.06, 1567.43) * mm, "end": v(8059.06, 1567.43) * mm});
            skLineSegment(sketch, "E42.4.0.3", {"start": v(7809.06, 1817.43) * mm, "end": v(7809.06, 1567.43) * mm});
            skLineSegment(sketch, "E42.5.0.0", {"start": v(8309.06, 1647.43) * mm, "end": v(8309.06, 1397.43) * mm});
            skLineSegment(sketch, "E42.5.0.1", {"start": v(8059.06, 1647.43) * mm, "end": v(8309.06, 1647.43) * mm});
            skLineSegment(sketch, "E42.5.0.2", {"start": v(8059.06, 1397.43) * mm, "end": v(8309.06, 1397.43) * mm});
            skLineSegment(sketch, "E42.5.0.3", {"start": v(8059.06, 1647.43) * mm, "end": v(8059.06, 1397.43) * mm});
            skLineSegment(sketch, "E42.6.0.0", {"start": v(8559.06, 1477.43) * mm, "end": v(8559.06, 1227.43) * mm});
            skLineSegment(sketch, "E42.6.0.1", {"start": v(8309.06, 1477.43) * mm, "end": v(8559.06, 1477.43) * mm});
            skLineSegment(sketch, "E42.6.0.2", {"start": v(8309.06, 1227.43) * mm, "end": v(8559.06, 1227.43) * mm});
            skLineSegment(sketch, "E42.6.0.3", {"start": v(8309.06, 1477.43) * mm, "end": v(8309.06, 1227.43) * mm});
            skLineSegment(sketch, "E42.7.0.0", {"start": v(8809.06, 1307.43) * mm, "end": v(8809.06, 1057.43) * mm});
            skLineSegment(sketch, "E42.7.0.1", {"start": v(8559.06, 1307.43) * mm, "end": v(8809.06, 1307.43) * mm});
            skLineSegment(sketch, "E42.7.0.2", {"start": v(8559.06, 1057.43) * mm, "end": v(8809.06, 1057.43) * mm});
            skLineSegment(sketch, "E42.7.0.3", {"start": v(8559.06, 1307.43) * mm, "end": v(8559.06, 1057.43) * mm});
            skLineSegment(sketch, "E42.direction1", {"start": v(6809.06, 2247.43) * mm, "end": v(7059.06, 2077.43) * mm, "construction": true});
            skSolve(sketch);
        }
        {
            var Q0;
            Q0=makeQuery(id+"F37.imprint","IMPRINT",FACE,{"disambiguationData":[TD([[makeQuery(id+"F37.imprint","IMPRINT",EDGE,{"derivedFrom":sQuery(id+"F37.wireOp",EDGE,"E42.7.0.0")}),-1.0]])]});
            var Q1;
            {var subQ4=sQuery(id+"F37.wireOp",EDGE,"E42.2.0.0");Q1=makeQuery(id+"F37.imprint","IMPRINT",FACE,{"disambiguationData":[TD([[makeQuery(id+"F37.imprint","IMPRINT",EDGE,{"derivedFrom":subQ4}),-1.0]])]});}
            var Q2;
            {var subQ4=sQuery(id+"F37.wireOp",EDGE,"E42.3.0.0");Q2=makeQuery(id+"F37.imprint","IMPRINT",FACE,{"disambiguationData":[TD([[makeQuery(id+"F37.imprint","IMPRINT",EDGE,{"derivedFrom":subQ4}),-1.0]])]});}
            var Q3;
            {var subQ4=sQuery(id+"F37.wireOp",EDGE,"E42.4.0.0");Q3=makeQuery(id+"F37.imprint","IMPRINT",FACE,{"disambiguationData":[TD([[makeQuery(id+"F37.imprint","IMPRINT",EDGE,{"derivedFrom":subQ4}),-1.0]])]});}
            var Q4;
            {var subQ4=sQuery(id+"F37.wireOp",EDGE,"E42.5.0.0");Q4=makeQuery(id+"F37.imprint","IMPRINT",FACE,{"disambiguationData":[TD([[makeQuery(id+"F37.imprint","IMPRINT",EDGE,{"derivedFrom":subQ4}),-1.0]])]});}
            var Q5;
            {var subQ4=sQuery(id+"F37.wireOp",EDGE,"E42.6.0.0");Q5=makeQuery(id+"F37.imprint","IMPRINT",FACE,{"disambiguationData":[TD([[makeQuery(id+"F37.imprint","IMPRINT",EDGE,{"derivedFrom":subQ4}),-1.0]])]});}
            var Q6;
            {var subQ3=sQuery(id+"F37.wireOp",EDGE,"E42.1.0.2");Q6=makeQuery(id+"F37.imprint","IMPRINT",FACE,{"disambiguationData":[TD([[makeQuery(id+"F37.imprint","IMPRINT",EDGE,{"derivedFrom":subQ3}),1.0]])]});}
            var Q7;
            {var subQ2=sQuery(id+"F37.wireOp",EDGE,"E42.1.0.1");Q7=makeQuery(id+"F37.imprint","IMPRINT",FACE,{"disambiguationData":[TD([[makeQuery(id+"F37.imprint","IMPRINT",EDGE,{"derivedFrom":subQ2}),-1.0]])]});}
            var Q8;
            {var subQ1=sQuery(id+"F37.wireOp",EDGE,"E40.bottom");Q8=makeQuery(id+"F37.imprint","IMPRINT",FACE,{"disambiguationData":[TD([[makeQuery(id+"F37.imprint","IMPRINT",EDGE,{"derivedFrom":subQ1}),1.0]])]});}
            var Q9;
            Q9=makeQuery(id+"F37.imprint","IMPRINT",FACE,{"disambiguationData":[TD([[makeQuery(id+"F37.imprint","IMPRINT",EDGE,{"derivedFrom":sQuery(id+"F37.wireOp",EDGE,"E41.bottom")}),-1.0]])]});
            extrude(context, id + "F38", {"entities" : qUnion([Q0, Q1, Q2, Q3, Q4, Q5, Q6, Q7, Q8, Q9]), "operationType" : NewBodyOperationType.ADD, "depth" : 900 * mm, "offsetDistance" : 25 * mm});
        }
        {
            var Q0;
            Q0=makeQuery(id+"F38.boolean.opBoolean","MERGE",FACE,{"derivedFrom":[makeQuery(id+"F34.opExtrude","SWEPT_FACE",FACE,{"disambiguationData":[OSD([sQuery(id+"F33.wireOp",EDGE,"E38.bottom")])]}),makeQuery(id+"F38.opExtrude","SWEPT_FACE",FACE,{"disambiguationData":[OSD([sQuery(id+"F37.wireOp",EDGE,"E40.bottom")])]})]});
            var sketch = newSketch(context, id + "F39", { "sketchPlane" : qUnion([Q0])});
            skLineSegment(sketch, "E43", {"start": v(543.74, 6009.06) * mm, "end": v(543.74, 8959.06) * mm});
            skLineSegment(sketch, "E44", {"start": v(543.74, 8959.06) * mm, "end": v(4843.74, 8959.06) * mm});
            skLineSegment(sketch, "E45", {"start": v(4843.74, 8959.06) * mm, "end": v(4843.74, 6742.77) * mm});
            skLineSegment(sketch, "E46.0", {"start": v(4703.74, 8819.06) * mm, "end": v(4703.74, 6742.77) * mm});
            skLineSegment(sketch, "E46.1", {"start": v(683.74, 8819.06) * mm, "end": v(4703.74, 8819.06) * mm});
            skLineSegment(sketch, "E46.2", {"start": v(683.74, 6009.06) * mm, "end": v(683.74, 8819.06) * mm});
            skLineSegment(sketch, "E47", {"start": v(543.74, 6009.06) * mm, "end": v(683.74, 6009.06) * mm});
            skLineSegment(sketch, "E48", {"start": v(4703.74, 6742.77) * mm, "end": v(4843.74, 6742.77) * mm});
            skLineSegment(sketch, "E49.bottom", {"start": v(5603.74, 6756.49) * mm, "end": v(5743.74, 6756.49) * mm});
            skLineSegment(sketch, "E49.top", {"start": v(5603.74, 6009.06) * mm, "end": v(5743.74, 6009.06) * mm});
            skLineSegment(sketch, "E49.left", {"start": v(5603.74, 6756.49) * mm, "end": v(5603.74, 6009.06) * mm});
            skLineSegment(sketch, "E49.right", {"start": v(5743.74, 6756.49) * mm, "end": v(5743.74, 6009.06) * mm});
            skSolve(sketch);
        }
        {
            var Q0;
            Q0=makeQuery(id+"F39.imprint","IMPRINT",FACE,{"disambiguationData":[TD([[makeQuery(id+"F39.imprint","IMPRINT",EDGE,{"derivedFrom":sQuery(id+"F39.wireOp",EDGE,"E43")}),-1.0]])]});
            var Q1;
            Q1=makeQuery(id+"F39.imprint","IMPRINT",FACE,{"disambiguationData":[TD([[makeQuery(id+"F39.imprint","IMPRINT",EDGE,{"derivedFrom":sQuery(id+"F39.wireOp",EDGE,"E49.bottom")}),-1.0]])]});
            extrude(context, id + "F40", {"entities" : qUnion([Q0, Q1]), "operationType" : NewBodyOperationType.ADD, "depth" : 900 * mm, "offsetDistance" : 25 * mm});
        }
        {
            var Q0;
            {var subQ5=sQuery(id+"F33.wireOp",EDGE,"E38.left");var subQ6=sQuery(id+"F33.wireOp",EDGE,"E38.bottom");Q0=makeQuery(id+"F38.boolean.opBoolean","SPLIT",FACE,{"disambiguationData":[TD([makeQuery(id+"F34.opExtrude","SWEPT_FACE",FACE,{"disambiguationData":[OSD([subQ6])]})])],"derivedFrom":makeQuery(id+"F34.opExtrude","SWEPT_FACE",FACE,{"disambiguationData":[OSD([subQ5])]})});}
            var sketch = newSketch(context, id + "F41", { "sketchPlane" : qUnion([Q0])});
            skLineSegment(sketch, "E50", {"start": v(6009.06, 5983.37) * mm, "end": v(9259.06, 4989.74) * mm});
            skLineSegment(sketch, "E51", {"start": v(9259.06, 4989.74) * mm, "end": v(9238.6, 4922.8) * mm});
            skLineSegment(sketch, "E52", {"start": v(9238.6, 4922.8) * mm, "end": v(6009.06, 5910.17) * mm});
            skLineSegment(sketch, "E53", {"start": v(6009.06, 5910.17) * mm, "end": v(6009.06, 5983.37) * mm});
            skLineSegment(sketch, "E54.bottom", {"start": v(8929.06, 5017.43) * mm, "end": v(8869.06, 5017.43) * mm});
            skLineSegment(sketch, "E54.top", {"start": v(8929.06, 4917.43) * mm, "end": v(8869.06, 4917.43) * mm});
            skLineSegment(sketch, "E54.left", {"start": v(8929.06, 5017.43) * mm, "end": v(8929.06, 4917.43) * mm});
            skLineSegment(sketch, "E54.right", {"start": v(8869.06, 5017.43) * mm, "end": v(8869.06, 4917.43) * mm});
            skSolve(sketch);
        }
        {
            var Q0;
            Q0 = qSketchRegion(id + "F41", true);
            var Q1;
            Q1=makeQuery(id+"F34.opExtrude","SWEPT_FACE",FACE,{"disambiguationData":[OSD([sQuery(id+"F33.wireOp",EDGE,"E38.right")])]});
            extrude(context, id + "F42", {"entities" : qUnion([Q0]), "operationType" : NewBodyOperationType.ADD, "endBound" : BoundingType.UP_TO_SURFACE, "oppositeDirection" : true, "depth" : 25 * mm, "endBoundEntityFace" : qUnion([Q1]), "offsetDistance" : 25 * mm});
        }
    });
